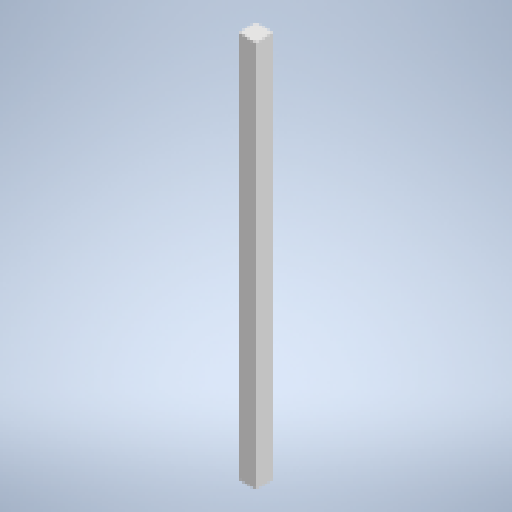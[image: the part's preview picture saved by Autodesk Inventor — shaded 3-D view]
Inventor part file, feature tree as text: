
AUTODESK INVENTOR PART (.ipt)
format: ipt  version: 2024 (Build 280153000, 153)  size: 137,728 bytes
history: native  units: mm
features: extrude x1, sketch x1
ambient origin geometry x8: Origin, YZ Plane, XZ Plane, XY Plane, X Axis, Y Axis, Z Axis, Center Point
bodies: Solid1 (feature_tree)
feature tree (2):
  extrude  "Extrusion1"  Depth=45.0mm
  sketch  "Sketch1"  dims[d0=45.0mm d1=45.0mm d2=1000.0mm d3=0.0mm]
